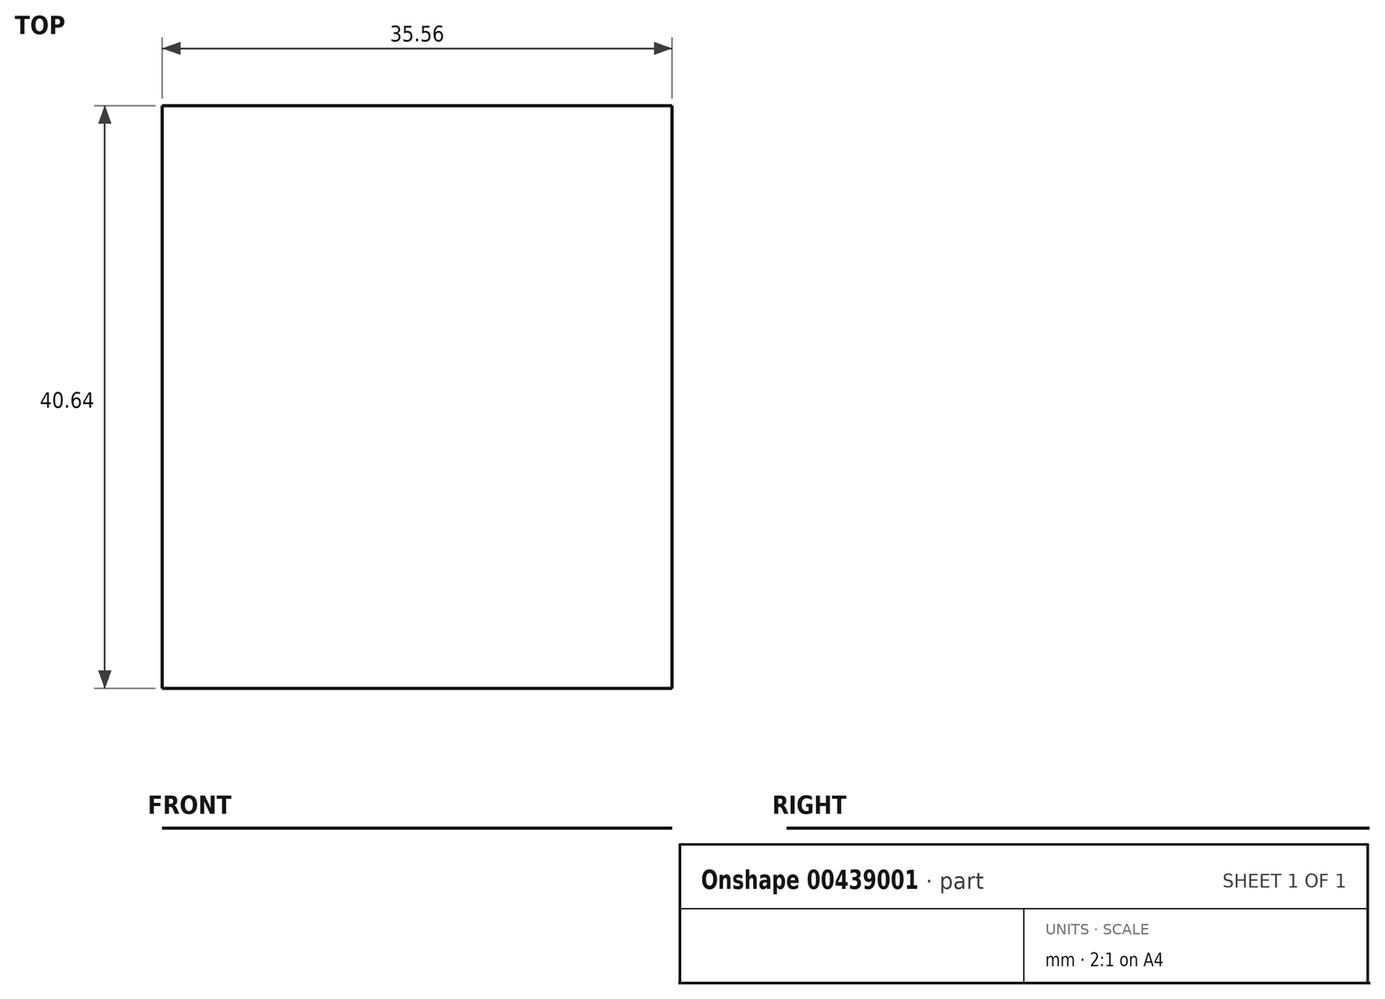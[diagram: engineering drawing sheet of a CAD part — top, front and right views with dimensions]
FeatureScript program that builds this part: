
annotation { "Feature Type Name" : "Feature", "Feature Type Description" : "" }
export const myFeature = defineFeature(function(context is Context, id is Id, definition is map)
    precondition{}
    {
        {
            var Q0;
            Q0=qCreatedBy(makeId("Top.planeOp"),FACE);
            var sketch = newSketch(context, id + "F0", { "sketchPlane" : qUnion([Q0])});
            skLineSegment(sketch, "E0.bottom", {"start": v(17.78, -20.32) * mm, "end": v(-17.78, -20.32) * mm});
            skLineSegment(sketch, "E0.top", {"start": v(17.78, 20.32) * mm, "end": v(-17.78, 20.32) * mm});
            skLineSegment(sketch, "E0.left", {"start": v(17.78, -20.32) * mm, "end": v(17.78, 20.32) * mm});
            skLineSegment(sketch, "E0.right", {"start": v(-17.78, -20.32) * mm, "end": v(-17.78, 20.32) * mm});
            skPoint(sketch, "E0.middle", {"position": v(0, 0) * mm});
            skSolve(sketch);
        }
        {
            var Q0;
            Q0=makeQuery(id+"F0.imprint","IMPRINT",FACE,{"disambiguationData":[TD([[makeQuery(id+"F0.imprint","IMPRINT",EDGE,{"derivedFrom":sQuery(id+"F0.wireOp",EDGE,"E0.bottom")}),-1.0]])]});
            extrude(context, id + "F1", {"entities" : qUnion([Q0]), "depth" : 1 / 203.2 * mm});
        }
        {
            var Q0;
            Q0=makeQuery(id+"F1.opExtrude","SWEPT_FACE",FACE,{"disambiguationData":[OSD([sQuery(id+"F0.wireOp",EDGE,"E0.right")])]});
            var sketch = newSketch(context, id + "F2", { "sketchPlane" : qUnion([Q0])});
            skLineSegment(sketch, "E1", {"start": v(0, 3.18) * mm, "end": v(0, 0) * mm, "construction": true});
            skLineSegment(sketch, "E2.bottom", {"start": v(12.7, 0) * mm, "end": v(-12.7, 0) * mm});
            skLineSegment(sketch, "E2.top", {"start": v(12.7, 3.17) * mm, "end": v(-12.7, 3.17) * mm});
            skLineSegment(sketch, "E2.left", {"start": v(12.7, 0) * mm, "end": v(12.7, 3.17) * mm});
            skLineSegment(sketch, "E2.right", {"start": v(-12.7, 0) * mm, "end": v(-12.7, 3.17) * mm});
            skPoint(sketch, "E2.middle", {"position": v(0, 1.59) * mm});
            skSolve(sketch);
        }
        {
            var Q0;
            Q0=makeQuery(id+"F2.imprint","IMPRINT",FACE,{"disambiguationData":[TD([[makeQuery(id+"F2.imprint","IMPRINT",EDGE,{"derivedFrom":sQuery(id+"F2.wireOp",EDGE,"E2.bottom")}),-1.0]])]});
            extrude(context, id + "F3", {"entities" : qUnion([Q0]), "operationType" : NewBodyOperationType.ADD, "depth" : 1 / 203.2 * mm});
        }
        {
            var Q0;
            Q0=makeQuery(id+"F1.opExtrude","SWEPT_FACE",FACE,{"disambiguationData":[OSD([sQuery(id+"F0.wireOp",EDGE,"E0.left")])]});
            var sketch = newSketch(context, id + "F4", { "sketchPlane" : qUnion([Q0])});
            skLineSegment(sketch, "E3", {"start": v(0, 3.18) * mm, "end": v(0, 0) * mm, "construction": true});
            skLineSegment(sketch, "E4.bottom", {"start": v(12.7, 0) * mm, "end": v(-12.7, 0) * mm});
            skLineSegment(sketch, "E4.top", {"start": v(12.7, 3.18) * mm, "end": v(-12.7, 3.18) * mm});
            skLineSegment(sketch, "E4.left", {"start": v(12.7, 0) * mm, "end": v(12.7, 3.18) * mm});
            skLineSegment(sketch, "E4.right", {"start": v(-12.7, 0) * mm, "end": v(-12.7, 3.18) * mm});
            skPoint(sketch, "E4.middle", {"position": v(0, 1.59) * mm});
            skSolve(sketch);
        }
        {
            var Q0;
            Q0=makeQuery(id+"F4.imprint","IMPRINT",FACE,{"disambiguationData":[TD([[makeQuery(id+"F4.imprint","IMPRINT",EDGE,{"derivedFrom":sQuery(id+"F4.wireOp",EDGE,"E4.bottom")}),1.0]])]});
            extrude(context, id + "F5", {"entities" : qUnion([Q0]), "operationType" : NewBodyOperationType.ADD, "depth" : 1 / 203.2 * mm});
        }
    });
